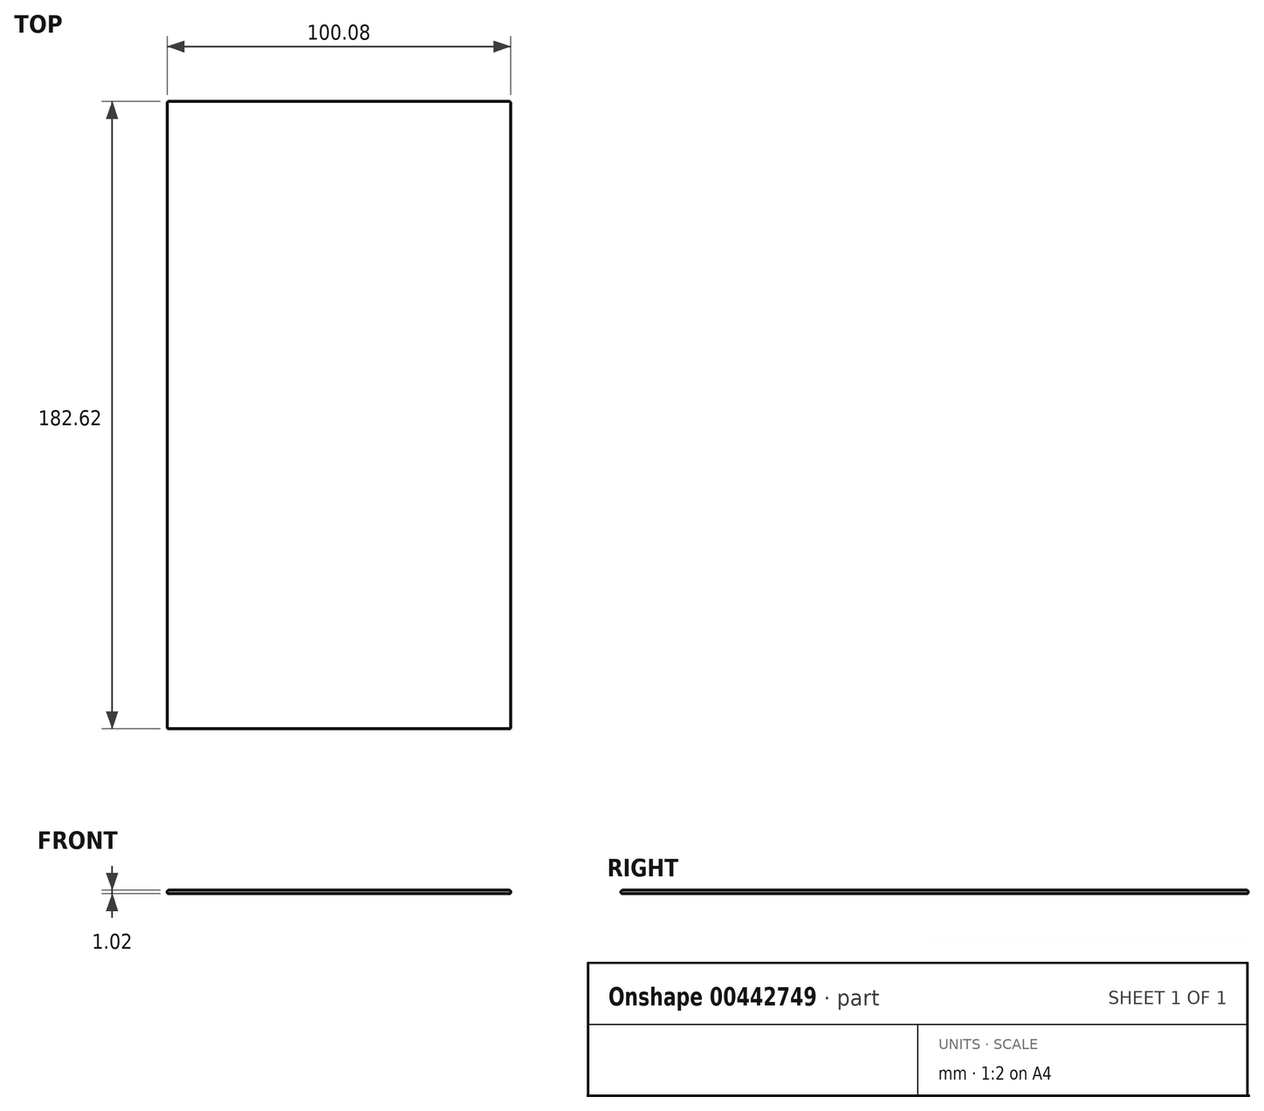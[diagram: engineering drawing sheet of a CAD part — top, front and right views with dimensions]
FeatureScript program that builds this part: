
annotation { "Feature Type Name" : "Feature", "Feature Type Description" : "" }
export const myFeature = defineFeature(function(context is Context, id is Id, definition is map)
    precondition{}
    {
        {
            var Q0;
            Q0=qCreatedBy(makeId("Top.planeOp"),FACE);
            var sketch = newSketch(context, id + "F0", { "sketchPlane" : qUnion([Q0])});
            skLineSegment(sketch, "E0.bottom", {"start": v(50.04, 91.31) * mm, "end": v(-50.04, 91.31) * mm});
            skLineSegment(sketch, "E0.top", {"start": v(50.04, -91.31) * mm, "end": v(-50.04, -91.31) * mm});
            skLineSegment(sketch, "E0.left", {"start": v(50.04, 91.31) * mm, "end": v(50.04, -91.31) * mm});
            skLineSegment(sketch, "E0.right", {"start": v(-50.04, 91.31) * mm, "end": v(-50.04, -91.31) * mm});
            skPoint(sketch, "E0.middle", {"position": v(0, 0) * mm});
            skSolve(sketch);
        }
        {
            var Q0;
            Q0 = qSketchRegion(id + "F0", true);
            extrude(context, id + "F1", {"entities" : qUnion([Q0]), "depth" : 1.02 * mm, "offsetDistance" : 25.4 * mm});
        }
        {
            var Q0;
            Q0=makeQuery(id+"F1.opExtrude","SWEPT_FACE",FACE,{"disambiguationData":[OSD([sQuery(id+"F0.wireOp",EDGE,"E0.left")])]});
            var Q1;
            Q1=makeQuery(id+"F1.opExtrude","SWEPT_FACE",FACE,{"disambiguationData":[OSD([sQuery(id+"F0.wireOp",EDGE,"E0.top")])]});
            var Q2;
            Q2=makeQuery(id+"F1.opExtrude","SWEPT_FACE",FACE,{"disambiguationData":[OSD([sQuery(id+"F0.wireOp",EDGE,"E0.right")])]});
            var Q3;
            Q3=makeQuery(id+"F1.opExtrude","SWEPT_FACE",FACE,{"disambiguationData":[OSD([sQuery(id+"F0.wireOp",EDGE,"E0.bottom")])]});
            fillet(context, id + "F2", {"entities" : qUnion([Q0, Q1, Q2, Q3]), "radius" : 0.5 * mm, "tangentPropagation" : true, "allowEdgeOverflow" : false});
        }
    });
